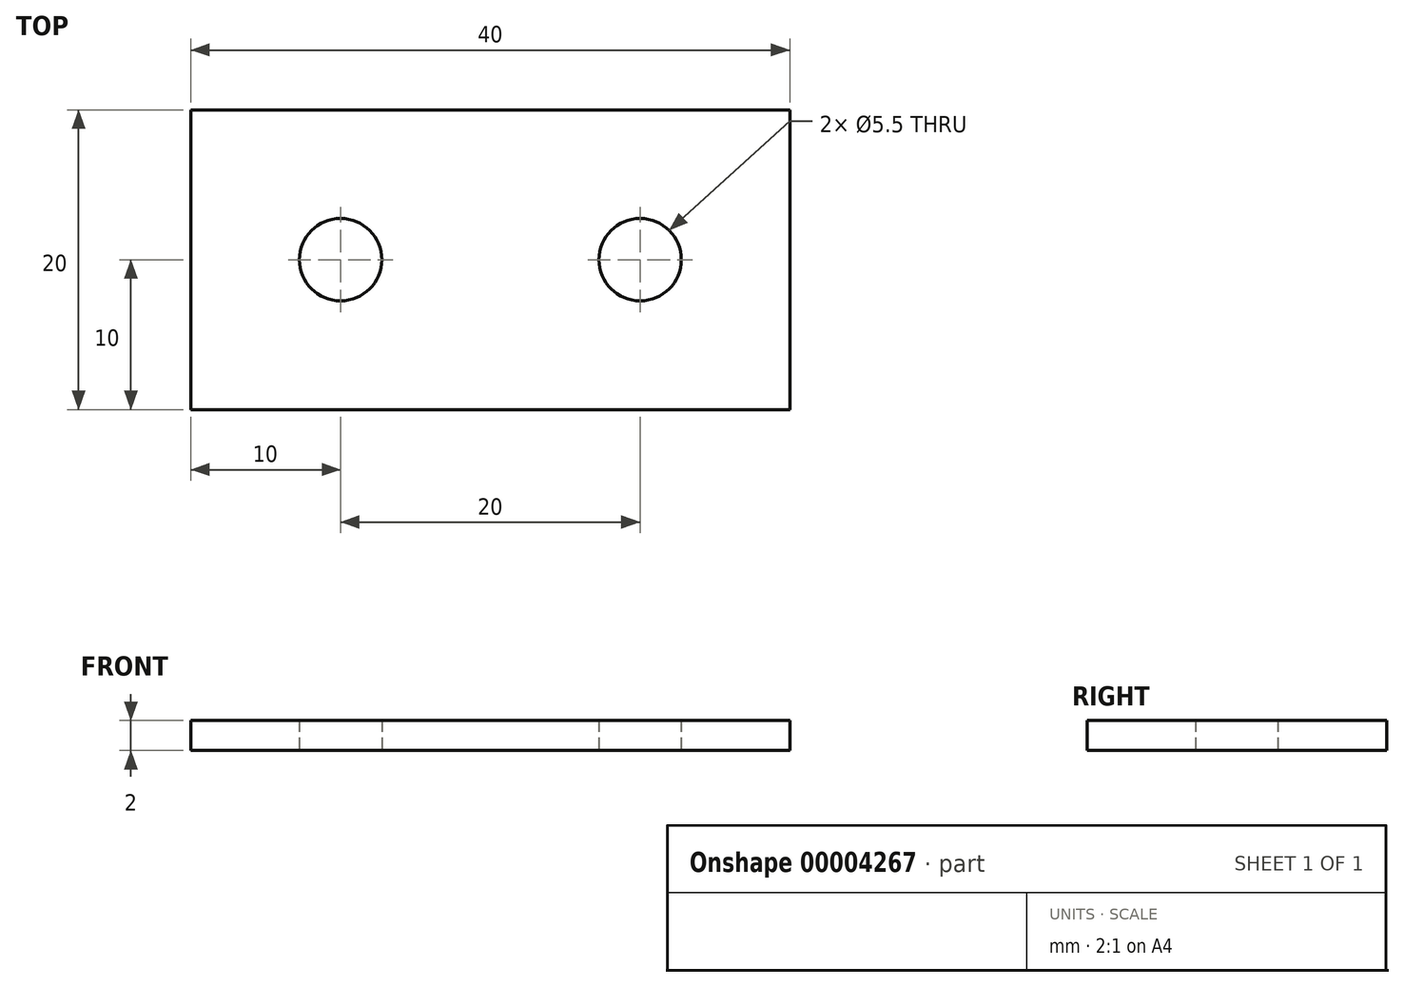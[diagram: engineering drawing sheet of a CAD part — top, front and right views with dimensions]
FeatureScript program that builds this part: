
annotation { "Feature Type Name" : "Feature", "Feature Type Description" : "" }
export const myFeature = defineFeature(function(context is Context, id is Id, definition is map)
    precondition{}
    {
        {
            var Q0;
            Q0=qCreatedBy(makeId("Top.planeOp"),FACE);
            var sketch = newSketch(context, id + "F0", { "sketchPlane" : qUnion([Q0])});
            skLineSegment(sketch, "E0.bottom", {"start": v(-20, 10) * mm, "end": v(20, 10) * mm});
            skLineSegment(sketch, "E0.top", {"start": v(-20, -10) * mm, "end": v(20, -10) * mm});
            skLineSegment(sketch, "E0.left", {"start": v(-20, 10) * mm, "end": v(-20, -10) * mm});
            skLineSegment(sketch, "E0.right", {"start": v(20, 10) * mm, "end": v(20, -10) * mm});
            skLineSegment(sketch, "E1", {"start": v(-20, 0) * mm, "end": v(0, 0) * mm, "construction": true});
            skLineSegment(sketch, "E2", {"start": v(0, 0) * mm, "end": v(20, 0) * mm, "construction": true});
            skPoint(sketch, "E3", {"position": v(-10, 0) * mm});
            skPoint(sketch, "E4", {"position": v(10, 0) * mm});
            skCircle(sketch, "E5", {"center": v(-10, 0) * mm, "radius": 2.75 * mm});
            skCircle(sketch, "E6", {"center": v(10, 0) * mm, "radius": 2.75 * mm});
            skSolve(sketch);
        }
        {
            var Q0;
            Q0=makeQuery(id+"F0.imprint","IMPRINT",FACE,{"disambiguationData":[TD([[makeQuery(id+"F0.imprint","IMPRINT",EDGE,{"derivedFrom":sQuery(id+"F0.wireOp",EDGE,"E0.bottom")}),-1.0]])]});
            extrude(context, id + "F1", {"entities" : qUnion([Q0]), "depth" : 2 * mm});
        }
    });
